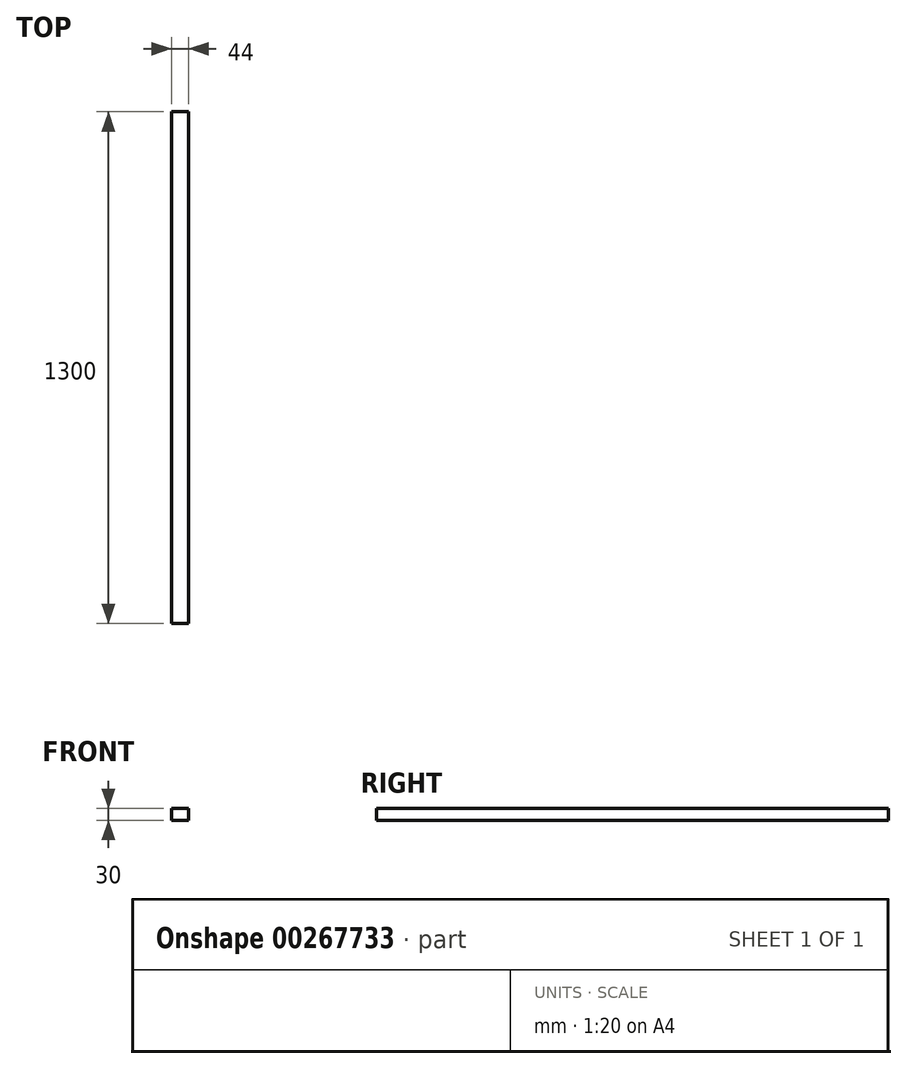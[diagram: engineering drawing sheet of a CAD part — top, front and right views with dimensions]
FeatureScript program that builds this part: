
annotation { "Feature Type Name" : "Feature", "Feature Type Description" : "" }
export const myFeature = defineFeature(function(context is Context, id is Id, definition is map)
    precondition{}
    {
        {
            var Q0;
            Q0=qCreatedBy(makeId("Front.planeOp"),FACE);
            var sketch = newSketch(context, id + "F0", { "sketchPlane" : qUnion([Q0])});
            skLineSegment(sketch, "E0.bottom", {"start": v(22, -15) * mm, "end": v(-22, -15) * mm});
            skLineSegment(sketch, "E0.top", {"start": v(22, 15) * mm, "end": v(-22, 15) * mm});
            skLineSegment(sketch, "E0.left", {"start": v(22, -15) * mm, "end": v(22, 15) * mm});
            skLineSegment(sketch, "E0.right", {"start": v(-22, -15) * mm, "end": v(-22, 15) * mm});
            skPoint(sketch, "E0.middle", {"position": v(0, 0) * mm});
            skSolve(sketch);
        }
        {
            var Q0;
            Q0 = qSketchRegion(id + "F0", true);
            extrude(context, id + "F1", {"entities" : qUnion([Q0]), "oppositeDirection" : true, "depth" : 1300 * mm});
        }
    });
